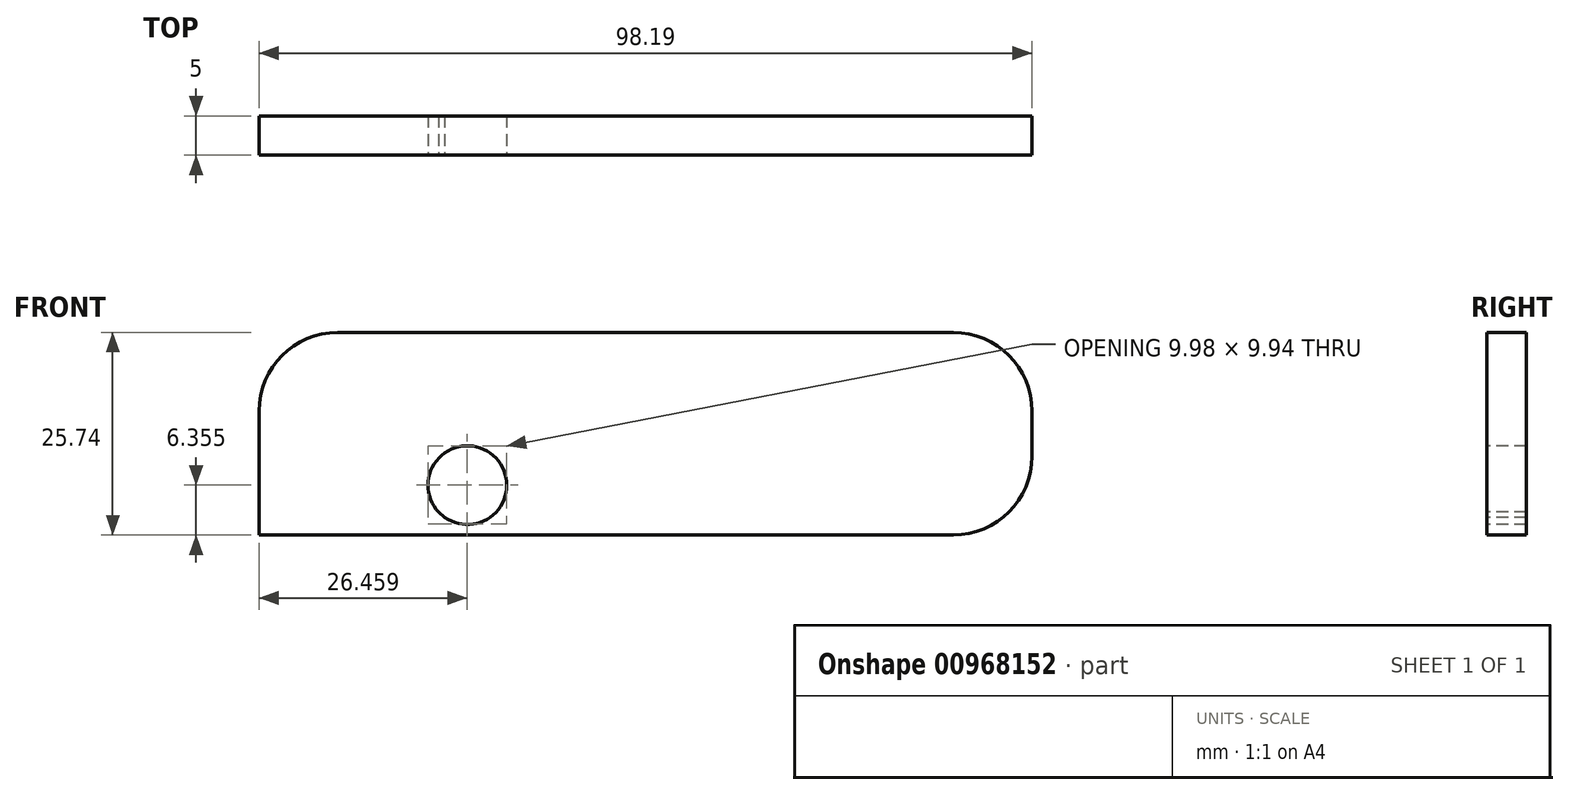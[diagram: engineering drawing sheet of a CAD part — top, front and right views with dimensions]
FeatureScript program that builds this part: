
annotation { "Feature Type Name" : "Feature", "Feature Type Description" : "" }
export const myFeature = defineFeature(function(context is Context, id is Id, definition is map)
    precondition{}
    {
        {
            var Q0;
            Q0=qCreatedBy(makeId("Front.planeOp"),FACE);
            var sketch = newSketch(context, id + "F0", { "sketchPlane" : qUnion([Q0])});
            skLineSegment(sketch, "E0.bottom", {"start": v(-34.27, 0.14) * mm, "end": v(63.92, 0.14) * mm});
            skLineSegment(sketch, "E0.top", {"start": v(-34.27, 25.88) * mm, "end": v(63.92, 25.88) * mm});
            skLineSegment(sketch, "E0.left", {"start": v(-34.27, 0.14) * mm, "end": v(-34.27, 25.88) * mm});
            skLineSegment(sketch, "E0.right", {"start": v(63.92, 0.14) * mm, "end": v(63.92, 25.88) * mm});
            skSolve(sketch);
        }
        {
            var Q0;
            Q0=makeQuery(id+"F0.imprint","IMPRINT",FACE,{"disambiguationData":[TD([[makeQuery(id+"F0.imprint","IMPRINT",EDGE,{"derivedFrom":sQuery(id+"F0.wireOp",EDGE,"E0.bottom")}),1.0]])]});
            extrude(context, id + "F1", {"entities" : qUnion([Q0]), "depth" : 5 * mm, "offsetDistance" : 25.4 * mm});
        }
        {
            var Q0;
            Q0=makeQuery(id+"F1.opExtrude","SWEPT_EDGE",EDGE,{"disambiguationData":[OSD([sQuery(id+"F0.wireOp",EDGE,"E0.top"),sQuery(id+"F0.wireOp",EDGE,"E0.right")])]});
            fillet(context, id + "F2", {"entities" : qUnion([Q0]), "radius" : 10 * mm, "tangentPropagation" : true, "allowEdgeOverflow" : false});
        }
        {
            var Q0;
            Q0=makeQuery(id+"F1.opExtrude","SWEPT_EDGE",EDGE,{"disambiguationData":[OSD([sQuery(id+"F0.wireOp",EDGE,"E0.bottom"),sQuery(id+"F0.wireOp",EDGE,"E0.right")])]});
            fillet(context, id + "F3", {"entities" : qUnion([Q0]), "radius" : 10 * mm, "tangentPropagation" : true, "allowEdgeOverflow" : false});
        }
        {
            var Q0;
            Q0=makeQuery(id+"F1.opExtrude","SWEPT_EDGE",EDGE,{"disambiguationData":[OSD([sQuery(id+"F0.wireOp",EDGE,"E0.top"),sQuery(id+"F0.wireOp",EDGE,"E0.left")])]});
            fillet(context, id + "F4", {"entities" : qUnion([Q0]), "radius" : 10 * mm, "tangentPropagation" : true, "allowEdgeOverflow" : false});
        }
        {
            var Q0;
            Q0=makeQuery(id+"F1.opExtrude","CAP_FACE",FACE,{"disambiguationData":[OSD([sQuery(id+"F0.wireOp",EDGE,"E0.bottom"),sQuery(id+"F0.wireOp",EDGE,"E0.top"),sQuery(id+"F0.wireOp",EDGE,"E0.left"),sQuery(id+"F0.wireOp",EDGE,"E0.right")])],"isStart":false});
            var sketch = newSketch(context, id + "F5", { "sketchPlane" : qUnion([Q0])});
            skCircle(sketch, "E1", {"center": v(-7.8, 6.47) * mm, "radius": 5 * mm});
            skLineSegment(sketch, "E2", {"start": v(-10.83, 10.45) * mm, "end": v(-34.27, 0.14) * mm});
            skLineSegment(sketch, "E3", {"start": v(-11.44, 3.04) * mm, "end": v(-8.1, 0.14) * mm});
            skSolve(sketch);
        }
        {
            var Q0;
            {var subQ0=sQuery(id+"F5.wireOp",EDGE,"E1");var subQ1=makeQuery(id+"F5.imprint","INTERSECT",VERTEX,{"derivedFrom":[subQ0,sQuery(id+"F5.wireOp",EDGE,"E2")]});Q0=makeQuery(id+"F5.imprint","IMPRINT",FACE,{"disambiguationData":[TD([[makeQuery(id+"F5.imprint","IMPRINT",EDGE,{"disambiguationData":[TD([[subQ1,-1.0]])],"derivedFrom":subQ0}),1.0]])]});}
            extrude(context, id + "F6", {"entities" : qUnion([Q0]), "operationType" : NewBodyOperationType.REMOVE, "endBound" : BoundingType.THROUGH_ALL, "oppositeDirection" : true, "depth" : 25 * mm, "offsetDistance" : 25 * mm});
        }
    });
